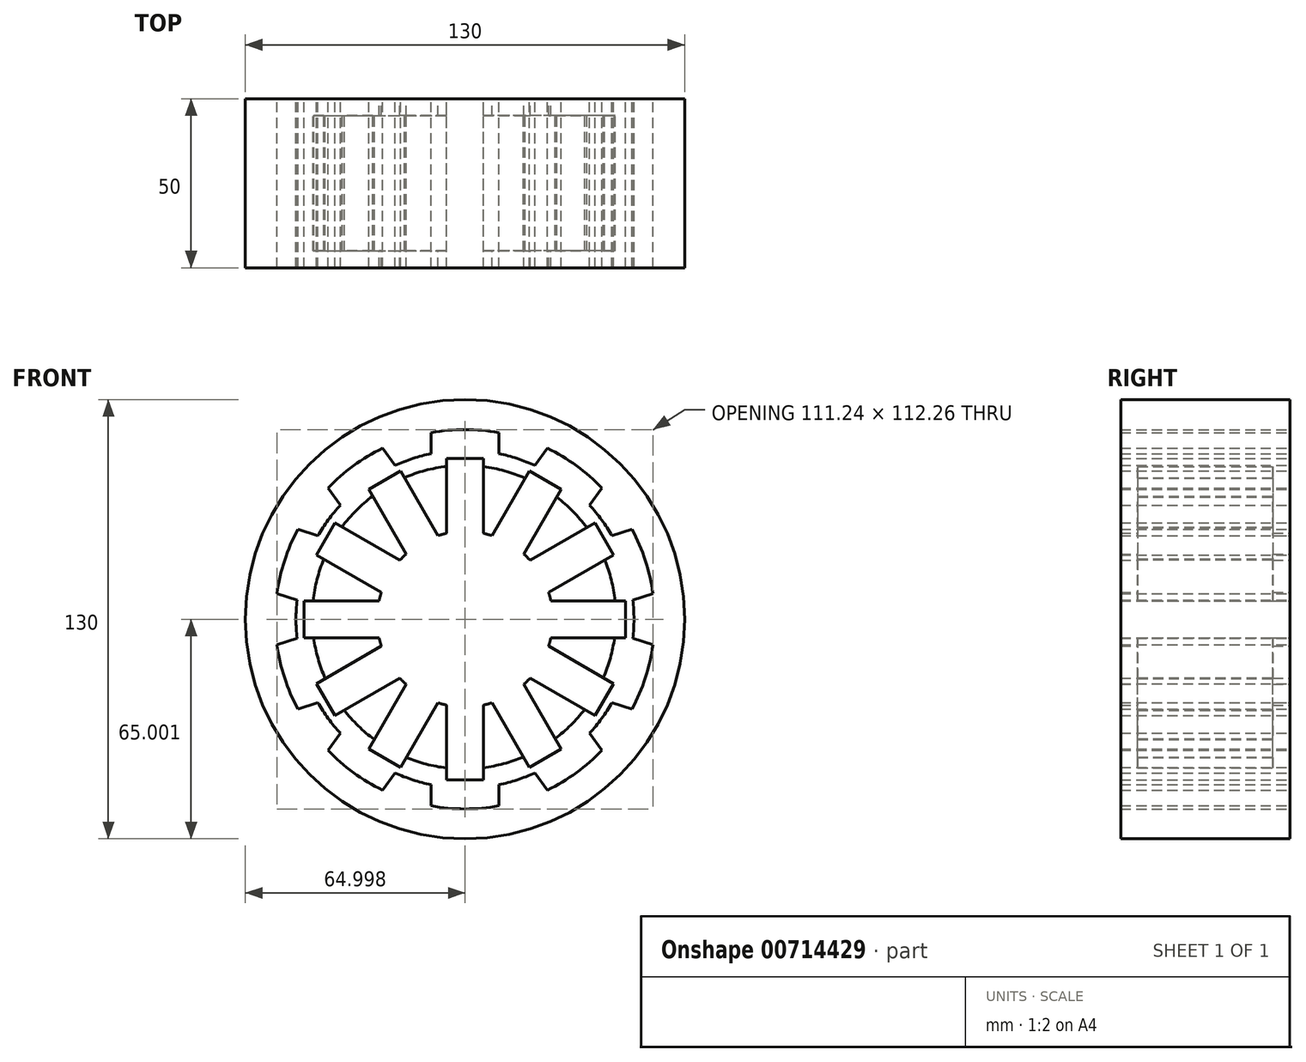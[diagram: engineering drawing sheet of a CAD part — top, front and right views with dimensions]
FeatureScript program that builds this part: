
annotation { "Feature Type Name" : "Feature", "Feature Type Description" : "" }
export const myFeature = defineFeature(function(context is Context, id is Id, definition is map)
    precondition{}
    {
        {
            var Q0;
            Q0=qCreatedBy(makeId("Front.planeOp"),FACE);
            var sketch = newSketch(context, id + "F0", { "sketchPlane" : qUnion([Q0])});
            skLineSegment(sketch, "E0.left", {"start": v(-130.96, 40.1) * mm, "end": v(-130.96, 33.86) * mm});
            skLineSegment(sketch, "E0.right", {"start": v(-110.96, 40.1) * mm, "end": v(-110.96, 33.86) * mm});
            skLineSegment(sketch, "E1.1.0", {"start": v(-145.34, 35.43) * mm, "end": v(-141.67, 30.38) * mm});
            skLineSegment(sketch, "E1.1.3", {"start": v(-161.52, 23.68) * mm, "end": v(-157.85, 18.63) * mm});
            skLineSegment(sketch, "E1.2.0", {"start": v(-170.4, 11.45) * mm, "end": v(-164.46, 9.52) * mm});
            skLineSegment(sketch, "E1.2.3", {"start": v(-176.58, -7.57) * mm, "end": v(-170.64, -9.5) * mm});
            skLineSegment(sketch, "E1.3.0", {"start": v(-176.58, -22.69) * mm, "end": v(-170.64, -20.76) * mm});
            skLineSegment(sketch, "E1.3.3", {"start": v(-170.4, -41.7) * mm, "end": v(-164.46, -39.78) * mm});
            skLineSegment(sketch, "E1.4.0", {"start": v(-161.52, -53.94) * mm, "end": v(-157.85, -48.89) * mm});
            skLineSegment(sketch, "E1.4.3", {"start": v(-145.34, -65.7) * mm, "end": v(-141.67, -60.64) * mm});
            skLineSegment(sketch, "E1.5.0", {"start": v(-130.96, -70.36) * mm, "end": v(-130.96, -64.12) * mm});
            skLineSegment(sketch, "E1.5.3", {"start": v(-110.96, -70.36) * mm, "end": v(-110.96, -64.12) * mm});
            skLineSegment(sketch, "E1.6.0", {"start": v(-96.59, -65.7) * mm, "end": v(-100.26, -60.64) * mm});
            skLineSegment(sketch, "E1.6.3", {"start": v(-80.4, -53.94) * mm, "end": v(-84.08, -48.89) * mm});
            skLineSegment(sketch, "E1.7.0", {"start": v(-71.52, -41.7) * mm, "end": v(-77.46, -39.78) * mm});
            skLineSegment(sketch, "E1.7.3", {"start": v(-65.34, -22.69) * mm, "end": v(-71.28, -20.76) * mm});
            skLineSegment(sketch, "E1.8.0", {"start": v(-65.34, -7.57) * mm, "end": v(-71.28, -9.5) * mm});
            skLineSegment(sketch, "E1.8.3", {"start": v(-71.52, 11.45) * mm, "end": v(-77.46, 9.52) * mm});
            skLineSegment(sketch, "E1.9.0", {"start": v(-80.4, 23.68) * mm, "end": v(-84.08, 18.63) * mm});
            skLineSegment(sketch, "E1.9.3", {"start": v(-96.59, 35.43) * mm, "end": v(-100.26, 30.38) * mm});
            skArc(sketch, "E2", {"start": v(-130.96, 33.86) * mm, "mid": v(-136.41, 32.42) * mm, "end": v(-141.67, 30.38) * mm});
            skCircle(sketch, "E3", {"center": v(-120.96, -15.13) * mm, "radius": 65 * mm});
            skArc(sketch, "E4", {"start": v(-145.34, 35.43) * mm, "mid": v(-153.95, 30.28) * mm, "end": v(-161.52, 23.68) * mm});
            skArc(sketch, "E5.trimOffspring", {"start": v(-157.85, 18.63) * mm, "mid": v(-161.41, 14.26) * mm, "end": v(-164.46, 9.52) * mm});
            skArc(sketch, "E6.trimOffspring", {"start": v(-170.64, -9.5) * mm, "mid": v(-170.96, -15.13) * mm, "end": v(-170.64, -20.76) * mm});
            skArc(sketch, "E7.trimOffspring", {"start": v(-164.46, -39.78) * mm, "mid": v(-161.41, -44.52) * mm, "end": v(-157.85, -48.89) * mm});
            skArc(sketch, "E8.trimOffspring", {"start": v(-141.67, -60.64) * mm, "mid": v(-136.41, -62.68) * mm, "end": v(-130.96, -64.12) * mm});
            skArc(sketch, "E9.trimOffspring", {"start": v(-110.96, -64.12) * mm, "mid": v(-105.51, -62.68) * mm, "end": v(-100.26, -60.64) * mm});
            skArc(sketch, "E10.trimOffspring", {"start": v(-84.08, -48.89) * mm, "mid": v(-80.51, -44.52) * mm, "end": v(-77.46, -39.78) * mm});
            skArc(sketch, "E11.trimOffspring", {"start": v(-71.28, -20.76) * mm, "mid": v(-70.96, -15.13) * mm, "end": v(-71.28, -9.5) * mm});
            skArc(sketch, "E12.trimOffspring", {"start": v(-77.46, 9.52) * mm, "mid": v(-80.51, 14.26) * mm, "end": v(-84.08, 18.63) * mm});
            skArc(sketch, "E13.trimOffspring", {"start": v(-100.26, 30.38) * mm, "mid": v(-105.51, 32.42) * mm, "end": v(-110.96, 33.86) * mm});
            skArc(sketch, "E14.trimOffspring", {"start": v(-110.96, 40.1) * mm, "mid": v(-120.96, 41) * mm, "end": v(-130.96, 40.1) * mm});
            skArc(sketch, "E15.trimOffspring", {"start": v(-80.4, 23.68) * mm, "mid": v(-87.97, 30.28) * mm, "end": v(-96.59, 35.43) * mm});
            skArc(sketch, "E16.trimOffspring", {"start": v(-65.34, -7.57) * mm, "mid": v(-67.58, 2.22) * mm, "end": v(-71.52, 11.45) * mm});
            skArc(sketch, "E17.trimOffspring", {"start": v(-71.52, -41.7) * mm, "mid": v(-67.58, -32.47) * mm, "end": v(-65.34, -22.69) * mm});
            skArc(sketch, "E18.trimOffspring", {"start": v(-96.59, -65.7) * mm, "mid": v(-87.97, -60.54) * mm, "end": v(-80.4, -53.94) * mm});
            skArc(sketch, "E19.trimOffspring", {"start": v(-130.96, -70.36) * mm, "mid": v(-120.96, -71.26) * mm, "end": v(-110.96, -70.36) * mm});
            skArc(sketch, "E20.trimOffspring", {"start": v(-161.52, -53.94) * mm, "mid": v(-153.95, -60.54) * mm, "end": v(-145.34, -65.7) * mm});
            skArc(sketch, "E21.trimOffspring", {"start": v(-176.58, -22.69) * mm, "mid": v(-174.35, -32.47) * mm, "end": v(-170.4, -41.7) * mm});
            skArc(sketch, "E22.trimOffspring", {"start": v(-170.4, 11.45) * mm, "mid": v(-174.35, 2.22) * mm, "end": v(-176.58, -7.57) * mm});
            skPoint(sketch, "E23.firstSnap0", {"position": v(-136.41, 32.42) * mm});
            skLineSegment(sketch, "E23.bottom", {"start": v(-120.96, 32.42) * mm, "end": v(-126.42, 32.42) * mm});
            skLineSegment(sketch, "E23.right", {"start": v(-126.42, 32.42) * mm, "end": v(-126.42, 10.28) * mm});
            skLineSegment(sketch, "E24.MirrorCS", {"start": v(-120.96, 32.42) * mm, "end": v(-115.5, 32.42) * mm});
            skLineSegment(sketch, "E25.MirrorCS", {"start": v(-115.5, 32.42) * mm, "end": v(-115.5, 10.28) * mm});
            skLineSegment(sketch, "E26.1.0", {"start": v(-140.01, 28.78) * mm, "end": v(-128.94, 9.6) * mm});
            skLineSegment(sketch, "E26.1.1", {"start": v(-144.74, 26.05) * mm, "end": v(-140.01, 28.78) * mm});
            skLineSegment(sketch, "E26.1.2", {"start": v(-144.74, 26.05) * mm, "end": v(-149.46, 23.33) * mm});
            skLineSegment(sketch, "E26.1.3", {"start": v(-149.46, 23.33) * mm, "end": v(-138.4, 4.15) * mm});
            skLineSegment(sketch, "E26.2.0", {"start": v(-159.42, 13.37) * mm, "end": v(-140.24, 2.3) * mm});
            skLineSegment(sketch, "E26.2.1", {"start": v(-162.14, 8.65) * mm, "end": v(-159.42, 13.37) * mm});
            skLineSegment(sketch, "E26.2.2", {"start": v(-162.14, 8.65) * mm, "end": v(-164.87, 3.92) * mm});
            skLineSegment(sketch, "E26.2.3", {"start": v(-164.87, 3.92) * mm, "end": v(-145.7, -7.15) * mm});
            skLineSegment(sketch, "E26.3.0", {"start": v(-168.51, -9.68) * mm, "end": v(-146.37, -9.68) * mm});
            skLineSegment(sketch, "E26.3.1", {"start": v(-168.51, -15.13) * mm, "end": v(-168.51, -9.68) * mm});
            skLineSegment(sketch, "E26.3.2", {"start": v(-168.51, -15.13) * mm, "end": v(-168.51, -20.58) * mm});
            skLineSegment(sketch, "E26.3.3", {"start": v(-168.51, -20.58) * mm, "end": v(-146.37, -20.58) * mm});
            skLineSegment(sketch, "E26.4.0", {"start": v(-164.87, -34.18) * mm, "end": v(-145.7, -23.11) * mm});
            skLineSegment(sketch, "E26.4.1", {"start": v(-162.14, -38.9) * mm, "end": v(-164.87, -34.18) * mm});
            skLineSegment(sketch, "E26.4.2", {"start": v(-162.14, -38.9) * mm, "end": v(-159.42, -43.63) * mm});
            skLineSegment(sketch, "E26.4.3", {"start": v(-159.42, -43.63) * mm, "end": v(-140.24, -32.56) * mm});
            skLineSegment(sketch, "E26.5.0", {"start": v(-149.46, -53.58) * mm, "end": v(-138.4, -34.4) * mm});
            skLineSegment(sketch, "E26.5.1", {"start": v(-144.74, -56.31) * mm, "end": v(-149.46, -53.58) * mm});
            skLineSegment(sketch, "E26.5.2", {"start": v(-144.74, -56.31) * mm, "end": v(-140.01, -59.04) * mm});
            skLineSegment(sketch, "E26.5.3", {"start": v(-140.01, -59.04) * mm, "end": v(-128.94, -39.86) * mm});
            skLineSegment(sketch, "E26.6.0", {"start": v(-126.42, -62.68) * mm, "end": v(-126.42, -40.54) * mm});
            skLineSegment(sketch, "E26.6.1", {"start": v(-120.96, -62.68) * mm, "end": v(-126.42, -62.68) * mm});
            skLineSegment(sketch, "E26.6.2", {"start": v(-120.96, -62.68) * mm, "end": v(-115.5, -62.68) * mm});
            skLineSegment(sketch, "E26.6.3", {"start": v(-115.5, -62.68) * mm, "end": v(-115.5, -40.54) * mm});
            skLineSegment(sketch, "E26.7.0", {"start": v(-101.9, -59.04) * mm, "end": v(-112.98, -39.86) * mm});
            skLineSegment(sketch, "E26.7.1", {"start": v(-97.19, -56.31) * mm, "end": v(-101.9, -59.04) * mm});
            skLineSegment(sketch, "E26.7.2", {"start": v(-97.19, -56.31) * mm, "end": v(-92.46, -53.58) * mm});
            skLineSegment(sketch, "E26.7.3", {"start": v(-92.46, -53.58) * mm, "end": v(-103.53, -34.4) * mm});
            skLineSegment(sketch, "E26.8.0", {"start": v(-82.5, -43.63) * mm, "end": v(-101.68, -32.56) * mm});
            skLineSegment(sketch, "E26.8.1", {"start": v(-79.78, -38.9) * mm, "end": v(-82.5, -43.63) * mm});
            skLineSegment(sketch, "E26.8.2", {"start": v(-79.78, -38.9) * mm, "end": v(-77.05, -34.18) * mm});
            skLineSegment(sketch, "E26.8.3", {"start": v(-77.05, -34.18) * mm, "end": v(-96.23, -23.11) * mm});
            skLineSegment(sketch, "E26.9.0", {"start": v(-73.4, -20.58) * mm, "end": v(-95.55, -20.58) * mm});
            skLineSegment(sketch, "E26.9.1", {"start": v(-73.4, -15.13) * mm, "end": v(-73.4, -20.58) * mm});
            skLineSegment(sketch, "E26.9.2", {"start": v(-73.4, -15.13) * mm, "end": v(-73.4, -9.68) * mm});
            skLineSegment(sketch, "E26.9.3", {"start": v(-73.4, -9.68) * mm, "end": v(-95.55, -9.68) * mm});
            skLineSegment(sketch, "E26.10.0", {"start": v(-77.05, 3.92) * mm, "end": v(-96.23, -7.15) * mm});
            skLineSegment(sketch, "E26.10.1", {"start": v(-79.78, 8.65) * mm, "end": v(-77.05, 3.92) * mm});
            skLineSegment(sketch, "E26.10.2", {"start": v(-79.78, 8.65) * mm, "end": v(-82.5, 13.37) * mm});
            skLineSegment(sketch, "E26.10.3", {"start": v(-82.5, 13.37) * mm, "end": v(-101.68, 2.3) * mm});
            skLineSegment(sketch, "E26.11.0", {"start": v(-92.46, 23.33) * mm, "end": v(-103.53, 4.15) * mm});
            skLineSegment(sketch, "E26.11.1", {"start": v(-97.19, 26.05) * mm, "end": v(-92.46, 23.33) * mm});
            skLineSegment(sketch, "E26.11.2", {"start": v(-97.19, 26.05) * mm, "end": v(-101.9, 28.78) * mm});
            skLineSegment(sketch, "E26.11.3", {"start": v(-101.9, 28.78) * mm, "end": v(-112.98, 9.6) * mm});
            skArc(sketch, "E27", {"start": v(-138.4, 4.15) * mm, "mid": v(-139.34, 3.25) * mm, "end": v(-140.24, 2.3) * mm});
            skArc(sketch, "E28.trimOffspring", {"start": v(-126.42, 10.28) * mm, "mid": v(-127.69, 9.97) * mm, "end": v(-128.94, 9.6) * mm});
            skArc(sketch, "E29.trimOffspring", {"start": v(-112.98, 9.6) * mm, "mid": v(-114.24, 9.97) * mm, "end": v(-115.5, 10.28) * mm});
            skArc(sketch, "E30.trimOffspring", {"start": v(-101.68, 2.3) * mm, "mid": v(-102.58, 3.25) * mm, "end": v(-103.53, 4.15) * mm});
            skArc(sketch, "E31.trimOffspring", {"start": v(-95.55, -9.68) * mm, "mid": v(-95.86, -8.4) * mm, "end": v(-96.23, -7.15) * mm});
            skArc(sketch, "E32.trimOffspring", {"start": v(-96.23, -23.11) * mm, "mid": v(-95.86, -21.86) * mm, "end": v(-95.55, -20.58) * mm});
            skArc(sketch, "E33.trimOffspring", {"start": v(-103.53, -34.4) * mm, "mid": v(-102.58, -33.5) * mm, "end": v(-101.68, -32.56) * mm});
            skArc(sketch, "E34.trimOffspring", {"start": v(-115.5, -40.54) * mm, "mid": v(-114.24, -40.23) * mm, "end": v(-112.98, -39.86) * mm});
            skArc(sketch, "E35.trimOffspring", {"start": v(-128.94, -39.86) * mm, "mid": v(-127.69, -40.23) * mm, "end": v(-126.42, -40.54) * mm});
            skArc(sketch, "E36.trimOffspring", {"start": v(-140.24, -32.56) * mm, "mid": v(-139.34, -33.5) * mm, "end": v(-138.4, -34.4) * mm});
            skArc(sketch, "E37.trimOffspring", {"start": v(-146.37, -20.58) * mm, "mid": v(-146.07, -21.86) * mm, "end": v(-145.7, -23.11) * mm});
            skArc(sketch, "E38.trimOffspring", {"start": v(-145.7, -7.15) * mm, "mid": v(-146.07, -8.4) * mm, "end": v(-146.37, -9.68) * mm});
            skSolve(sketch);
        }
        {
            var Q0;
            Q0=qCreatedBy(makeId("Front.planeOp"),FACE);
            var sketch = newSketch(context, id + "F1", { "sketchPlane" : qUnion([Q0])});
            skCircle(sketch, "E39", {"center": v(-121.22, -14.53) * mm, "radius": 44.92 * mm});
            skSolve(sketch);
        }
        {
            var Q0;
            Q0=makeQuery(id+"F0.imprint","IMPRINT",FACE,{"disambiguationData":[TD([[makeQuery(id+"F0.imprint","IMPRINT",EDGE,{"derivedFrom":sQuery(id+"F0.wireOp",EDGE,"E23.bottom")}),1.0]])]});
            extrude(context, id + "F2", {"entities" : qUnion([Q0]), "endBound" : BoundingType.SYMMETRIC, "depth" : 50 * mm, "offsetDistance" : 25 * mm});
        }
        {
            var Q0;
            Q0=makeQuery(id+"F0.imprint","IMPRINT",FACE,{"disambiguationData":[TD([[makeQuery(id+"F0.imprint","IMPRINT",EDGE,{"derivedFrom":sQuery(id+"F0.wireOp",EDGE,"E0.left")}),-1.0]])]});
            extrude(context, id + "F3", {"entities" : qUnion([Q0]), "endBound" : BoundingType.SYMMETRIC, "depth" : 50 * mm, "offsetDistance" : 25 * mm});
        }
        {
            var Q0;
            Q0=qSketchRegion(id+"F1",true);
            extrude(context, id + "F4", {"entities" : qUnion([Q0]), "operationType" : NewBodyOperationType.ADD, "endBound" : BoundingType.SYMMETRIC, "depth" : 40 * mm, "offsetDistance" : 25 * mm});
        }
    });
